# Revit family: FP-Revit20-en-RF505BRNQX1-RefrigeratorFreezer-900006117A-UK-IE-SG
name_source: partatom
category: Specialty Equipment
units: mm (PartAtom-declared; Revit-internal decimal feet)

## family parameters
Always vertical = No
Cut with Voids When Loaded = No
Part Type = Normal
Room Calculation Point = No
Round Connector Dimension = Use Diameter
Shared = No
Work Plane-Based = No

## types (1)
- RF505BRNQX1
    Clearance = Fisher & Paykel - Clearance Required (Non-Combustible)
    Clearance to back = 30 mm  [stored 0.0984252 ft]
    Clearance to sides = 20 mm  [stored 0.0656168 ft]
    Default Elevation = 0 mm  [stored 0 ft]
    Description = Refrigerator Freezer
    Electrical Specifications = Supply: 220V - 240V, 50Hz, Service: 10A circuit
    Handle Material = Fisher & Paykel - Grey, Charcoal
    Manufacturer = Fisher & Paykel
    Model = RF505BRNQX1
RF505BRNX1, RF505BRNB1, RF505BRNQX1
RF505BRNX1, RF505BRNB1, RF505BRNQX1
    Product Depth = 707 mm
    Product Height = 1726 mm  [stored 5.66273 ft]
    Product Width = 790 mm  [stored 2.59186 ft]
    URL = www.fisherpaykel.com
    Vent Clearance - See planning Guide for options = 50 mm  [stored 0.164042 ft]
    Water Dispenser Material = Fisher & Paykel - Black, Matte

note: [stored X ft] marks values corroborated as IEEE doubles in the binary element streams (Revit-internal decimal feet)

## geometry (parser evidence)
native form markers: Sweep x4
no freeform markers — native parametric forms only
